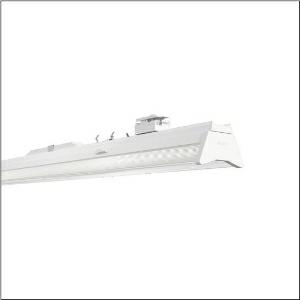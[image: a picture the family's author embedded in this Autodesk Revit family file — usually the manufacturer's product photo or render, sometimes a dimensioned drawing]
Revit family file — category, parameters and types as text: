
# Revit family: licross_r__21_performance_mo_52td16vn48xg_2cf7
name_source: partatom
category: Lighting Fixtures
units: mm (PartAtom-declared; Revit-internal decimal feet)

## family parameters
Cut with Voids When Loaded = No
Host = Face
Light Source = No
Part Type = Normal
Room Calculation Point = No
Round Connector Dimension = Use Diameter
Shared = No

## types (1)
- --- (1 x LED, 8000 lm, 44.6 W, 4000K)
    Apparent Load = 45 VA
    CIE Flux Codes = 66 88 96 79 100
    Color Rendering = 80
    Color Temperature = 4000K
    Default Elevation = 1800 mm
    Description = Licross® 21 Performance MO, luminaire insert, of sheet steel, galvanised, coil coated, white, length: 1.500mm, width: 120mm, height: 123mm, LED rated luminous flux: 8.000lm, light colour: 840, control gear: DALI 2, CLO, with plug, 5-pole, with phase selection, mains connection: 220..240V, AC, 50/60Hz, start of lifetime: 45W, end of service life: 53W, internal wiring halogen-free, primary light control with lens, of plastic, primary optical cover: cover, of PMMA, light emission: direct/indirect distribution, primary light characteristic: symmetric, protection rating (complete): IP54, insulation class (complete): insulation class I (protective earthing), certification: CE, ENEC, VDE, UKCA, protection symbol: D if used in an environment with non-conductive dust loads with corresponding accessories, impact resistance: IK06, permissible ambient temperature for indoor applications: -25..+45°C, corresponds to IFS (International Featured Standards) requirements for safety and quality in the food industry, reducing of maximum allowable ambient temperature of 5°C with ceiling mounting, LABS conformity tested according to VDMA 24364:2018-05, packaging unit: 1 piece
    Height = 114 mm
    Lamp = 1 x LED
    Lamp Light Flux = 8000 lm
    Lamp Power = 44.6 W
    Lamp count = 1
    Length = 1500 mm
    Luminous efficacy = 179 lm/W
    Manufacturer = Siteco
    ModVariant = No
    Model = 52TD16VN48XG
    Mounting Place = Ceiling
    Mounting Type = Pendant
    Number of Poles = 1
    OnlyDefault = Yes
    Power Factor = 1
    Product Name = Licross® 21 Performance MO
    Product group = luminaire insert | ceiling pendant
    ProductGroupID = 902
    Protection Class = Protection class I
    Protection Degree = IP 54
    RLX_Detail_Level = 1
    RLX_Emergency_Light_Flux = 0 lm
    RLX_Emergency_Type = 0
    RLX_Emergency_Type_DB = No
    RlxData = <blob elided: 34069 chars, md5=f113da53>
    Socket = socket
    Standby Power = 0 W
    System Light Flux = 8000 lm
    System Power = 45 W
    Type Comments = factory setting: luminous flux: 100 % | dim-lin: 254 | 301 mA
    Type Image = l_1256138.jpg
    URL = http://relux.com
    VarID = @adj_104543
    Voltage = 0 V
    Weight = 0.00 kg
    Width = 120 mm

## geometry (parser evidence)
native form markers: Blend x4, Sweep x13
no freeform markers — native parametric forms only
